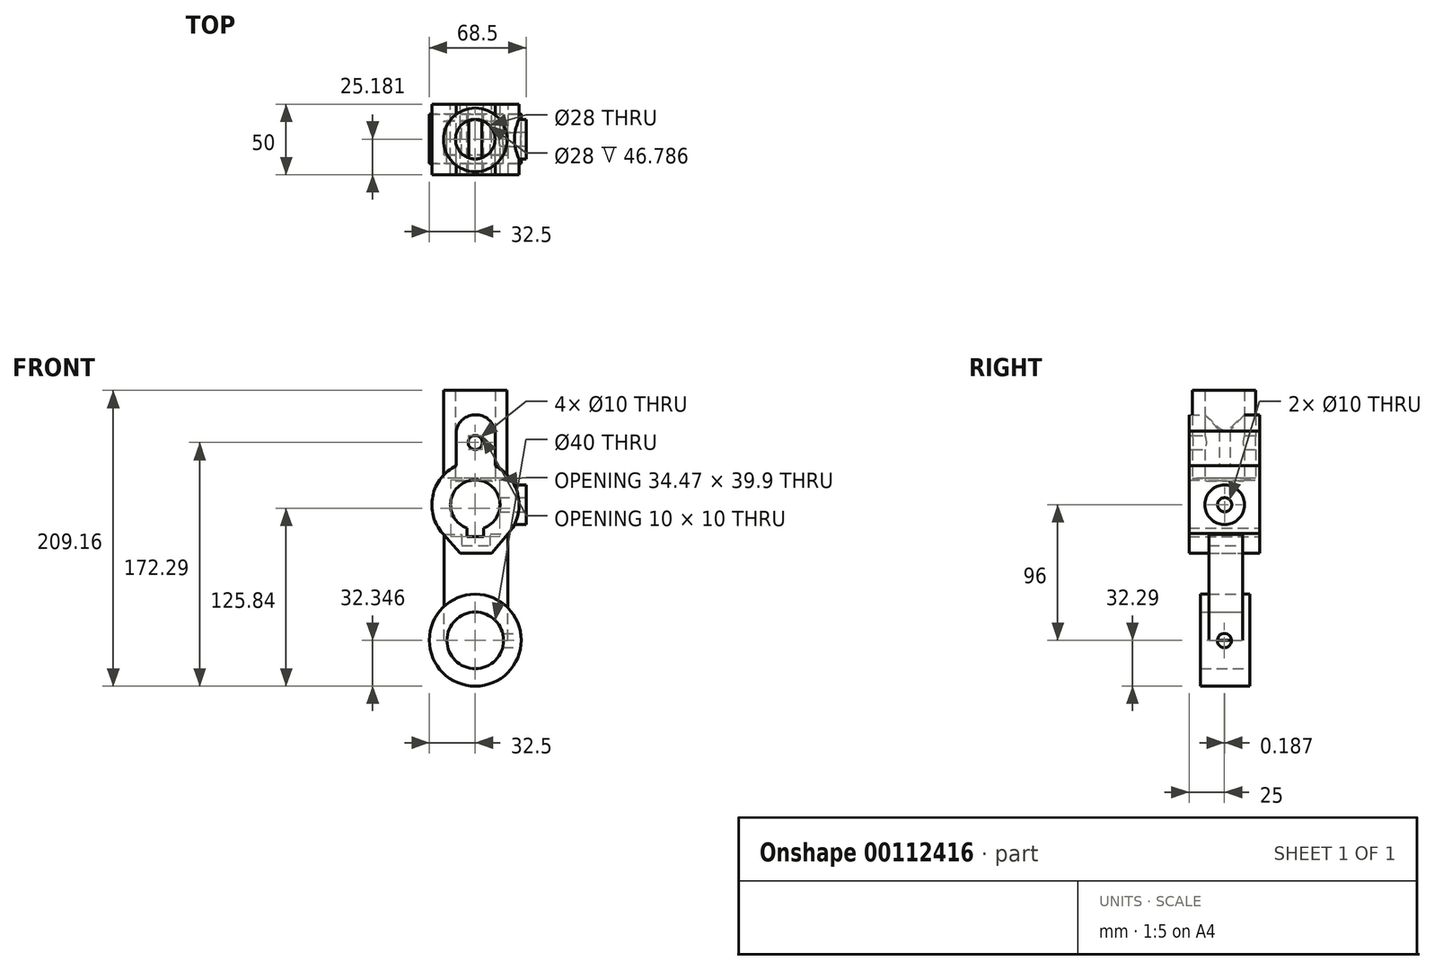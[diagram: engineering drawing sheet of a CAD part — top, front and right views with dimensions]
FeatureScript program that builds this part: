
annotation { "Feature Type Name" : "Feature", "Feature Type Description" : "" }
export const myFeature = defineFeature(function(context is Context, id is Id, definition is map)
    precondition{}
    {
        {
            var Q0;
            Q0=qCreatedBy(makeId("Front.planeOp"),FACE);
            var sketch = newSketch(context, id + "F0", { "sketchPlane" : qUnion([Q0])});
            skPoint(sketch, "E0.middle", {"position": v(0, 0) * mm});
            skCircle(sketch, "E1", {"center": v(0, -42.87) * mm, "radius": 32.5 * mm, "construction": true});
            skCircle(sketch, "E2", {"center": v(0, 97.13) * mm, "radius": 5 * mm});
            skArc(sketch, "E3", {"start": v(-6, 36.7) * mm, "mid": v(0, 70.63) * mm, "end": v(6, 36.7) * mm});
            skLineSegment(sketch, "E4", {"start": v(-6, 36.7) * mm, "end": v(-6, 30.73) * mm});
            skLineSegment(sketch, "E5", {"start": v(-6, 30.73) * mm, "end": v(6, 30.73) * mm});
            skLineSegment(sketch, "E6", {"start": v(6, 30.73) * mm, "end": v(6, 36.7) * mm});
            skArc(sketch, "E7", {"start": v(-23.07, 32.82) * mm, "mid": v(-30.14, 59.16) * mm, "end": v(-13.48, 80.76) * mm});
            skArc(sketch, "E8", {"start": v(14.05, 80.76) * mm, "mid": v(30.43, 59) * mm, "end": v(23.32, 32.72) * mm});
            skLineSegment(sketch, "E9", {"start": v(-13.48, 80.76) * mm, "end": v(-13.48, 105.36) * mm});
            skLineSegment(sketch, "E10", {"start": v(14.05, 80.76) * mm, "end": v(14.05, 105.36) * mm});
            skArc(sketch, "E11", {"start": v(14.05, 105.36) * mm, "mid": v(0.29, 116.78) * mm, "end": v(-13.48, 105.36) * mm});
            skLineSegment(sketch, "E12", {"start": v(-23.07, 32.82) * mm, "end": v(-10.66, 18.72) * mm});
            skLineSegment(sketch, "E13", {"start": v(-10.66, 18.72) * mm, "end": v(11.52, 18.72) * mm});
            skLineSegment(sketch, "E14", {"start": v(11.52, 18.72) * mm, "end": v(23.32, 32.72) * mm});
            skLineSegment(sketch, "E15", {"start": v(0, 53.13) * mm, "end": v(36, 53.13) * mm});
            skLineSegment(sketch, "E16", {"start": v(0, -42.87) * mm, "end": v(32.5, -42.87) * mm, "construction": true});
            skSolve(sketch);
        }
        {
            var Q0;
            Q0=qCreatedBy(makeId("Front.planeOp"),FACE);
            var sketch = newSketch(context, id + "F1", { "sketchPlane" : qUnion([Q0])});
            skLineSegment(sketch, "E17.bottom", {"start": v(-21.95, -42.74) * mm, "end": v(23.05, -42.74) * mm});
            skLineSegment(sketch, "E17.left", {"start": v(-21.95, -42.74) * mm, "end": v(-21.95, 32.26) * mm});
            skLineSegment(sketch, "E17.right", {"start": v(23.05, -42.74) * mm, "end": v(23.05, 32.26) * mm});
            skLineSegment(sketch, "E18", {"start": v(-21.95, 32.26) * mm, "end": v(-9.56, 32.26) * mm});
            skLineSegment(sketch, "E19", {"start": v(-9.56, 32.26) * mm, "end": v(-9.56, 24.09) * mm});
            skLineSegment(sketch, "E20", {"start": v(-9.56, 24.09) * mm, "end": v(10.73, 24.09) * mm});
            skLineSegment(sketch, "E21", {"start": v(10.73, 24.09) * mm, "end": v(10.73, 32.49) * mm});
            skLineSegment(sketch, "E22", {"start": v(10.73, 32.49) * mm, "end": v(23.05, 32.26) * mm});
            skSolve(sketch);
        }
        {
            var Q0;
            Q0 = qSketchRegion(id + "F0", true);
            extrude(context, id + "F2", {"entities" : qUnion([Q0]), "depth" : 50 * mm});
        }
        {
            var Q0;
            Q0 = qSketchRegion(id + "F1", true);
            extrude(context, id + "F3", {"entities" : qUnion([Q0]), "depth" : 36 * mm, "hasSecondDirection" : true, "secondDirectionOppositeDirection" : false, "secondDirectionDepth" : 12 * mm});
        }
        {
            var Q0;
            Q0=qCreatedBy(makeId("Front.planeOp"),FACE);
            var sketch = newSketch(context, id + "F4", { "sketchPlane" : qUnion([Q0])});
            skCircle(sketch, "E23", {"center": v(0, -42.66) * mm, "radius": 32.5 * mm});
            skSolve(sketch);
        }
        {
            var Q0;
            Q0 = qSketchRegion(id + "F4", true);
            extrude(context, id + "F5", {"entities" : qUnion([Q0]), "depth" : 42 * mm, "hasSecondDirection" : true, "secondDirectionOppositeDirection" : false, "secondDirectionDepth" : 7 * mm});
        }
        {
            var Q0;
            Q0=qCreatedBy(makeId("Top.planeOp"),FACE);
            var sketch = newSketch(context, id + "F6", { "sketchPlane" : qUnion([Q0])});
            skCircle(sketch, "E24", {"center": v(0, -25.31) * mm, "radius": 22.5 * mm});
            skSolve(sketch);
        }
        {
            var Q0;
            Q0 = qSketchRegion(id + "F6", true);
            var Q1;
            Q1=makeQuery(id+"F2.opExtrude","SWEPT_FACE",FACE,{"disambiguationData":[OSD([sQuery(id+"F0.wireOp",EDGE,"E2")])]});
            extrude(context, id + "F7", {"entities" : qUnion([Q0]), "depth" : 134 * mm, "hasSecondDirection" : true, "secondDirectionOppositeDirection" : false, "secondDirectionBoundEntityFace" : qUnion([Q1]), "secondDirectionDepth" : 72 * mm});
        }
        {
            var Q0;
            Q0=qCreatedBy(makeId("Top.planeOp"),FACE);
            var sketch = newSketch(context, id + "F8", { "sketchPlane" : qUnion([Q0])});
            skCircle(sketch, "E25", {"center": v(0, -24.82) * mm, "radius": 14 * mm});
            skSolve(sketch);
        }
        {
            var Q0;
            Q0 = qSketchRegion(id + "F8", true);
            extrude(context, id + "F9", {"entities" : qUnion([Q0]), "operationType" : NewBodyOperationType.REMOVE, "depth" : 134 * mm, "hasSecondDirection" : true, "secondDirectionOppositeDirection" : false, "secondDirectionDepth" : 70 * mm});
        }
        {
            var Q0;
            Q0=qCreatedBy(makeId("Front.planeOp"),FACE);
            var sketch = newSketch(context, id + "F10", { "sketchPlane" : qUnion([Q0])});
            skCircle(sketch, "E26", {"center": v(0, 97.13) * mm, "radius": 5 * mm});
            skSolve(sketch);
        }
        {
            var Q0;
            Q0 = qSketchRegion(id + "F10", true);
            extrude(context, id + "F11", {"entities" : qUnion([Q0]), "operationType" : NewBodyOperationType.REMOVE, "depth" : 50 * mm});
        }
        {
            var Q0;
            Q0=qCreatedBy(makeId("Front.planeOp"),FACE);
            var sketch = newSketch(context, id + "F12", { "sketchPlane" : qUnion([Q0])});
            skCircle(sketch, "E27", {"center": v(0, -42.81) * mm, "radius": 20 * mm});
            skSolve(sketch);
        }
        {
            var Q0;
            Q0 = qSketchRegion(id + "F12", true);
            extrude(context, id + "F13", {"entities" : qUnion([Q0]), "operationType" : NewBodyOperationType.REMOVE, "depth" : 50 * mm});
        }
        {
            var Q0;
            Q0=qCreatedBy(makeId("Right.planeOp"),FACE);
            cPlane(context, id + "F14", {"entities" : qUnion([Q0]), "cplaneType" : CPlaneType.OFFSET, "offset" : 36 * mm, "width" : 150 * mm, "height" : 150 * mm});
        }
        {
            var Q0;
            Q0=qCreatedBy(id+"F14.planeOp",FACE);
            var sketch = newSketch(context, id + "F15", { "sketchPlane" : qUnion([Q0])});
            skCircle(sketch, "E28", {"center": v(-24.81, 53.13) * mm, "radius": 14 * mm});
            skSolve(sketch);
        }
        {
            var Q0;
            Q0 = qSketchRegion(id + "F15", true);
            var Q1;
            Q1=makeQuery(id+"F2.opExtrude","SWEPT_FACE",FACE,{"disambiguationData":[OSD([sQuery(id+"F0.wireOp",EDGE,"E8")])]});
            extrude(context, id + "F16", {"entities" : qUnion([Q0]), "operationType" : NewBodyOperationType.ADD, "oppositeDirection" : true, "depth" : 9 * mm});
        }
        {
            var Q0;
            Q0=qCreatedBy(id+"F14.planeOp",FACE);
            var sketch = newSketch(context, id + "F17", { "sketchPlane" : qUnion([Q0])});
            skCircle(sketch, "E29", {"center": v(-24.81, 53.13) * mm, "radius": 5 * mm});
            skCircle(sketch, "E30", {"center": v(-25, -42.87) * mm, "radius": 5 * mm});
            skLineSegment(sketch, "E31", {"start": v(0, -42.87) * mm, "end": v(-25, -42.87) * mm, "construction": true});
            skSolve(sketch);
        }
        {
            var Q0;
            Q0 = qSketchRegion(id + "F17", true);
            extrude(context, id + "F18", {"entities" : qUnion([Q0]), "operationType" : NewBodyOperationType.REMOVE, "oppositeDirection" : true, "depth" : 25 * mm});
        }
    });
